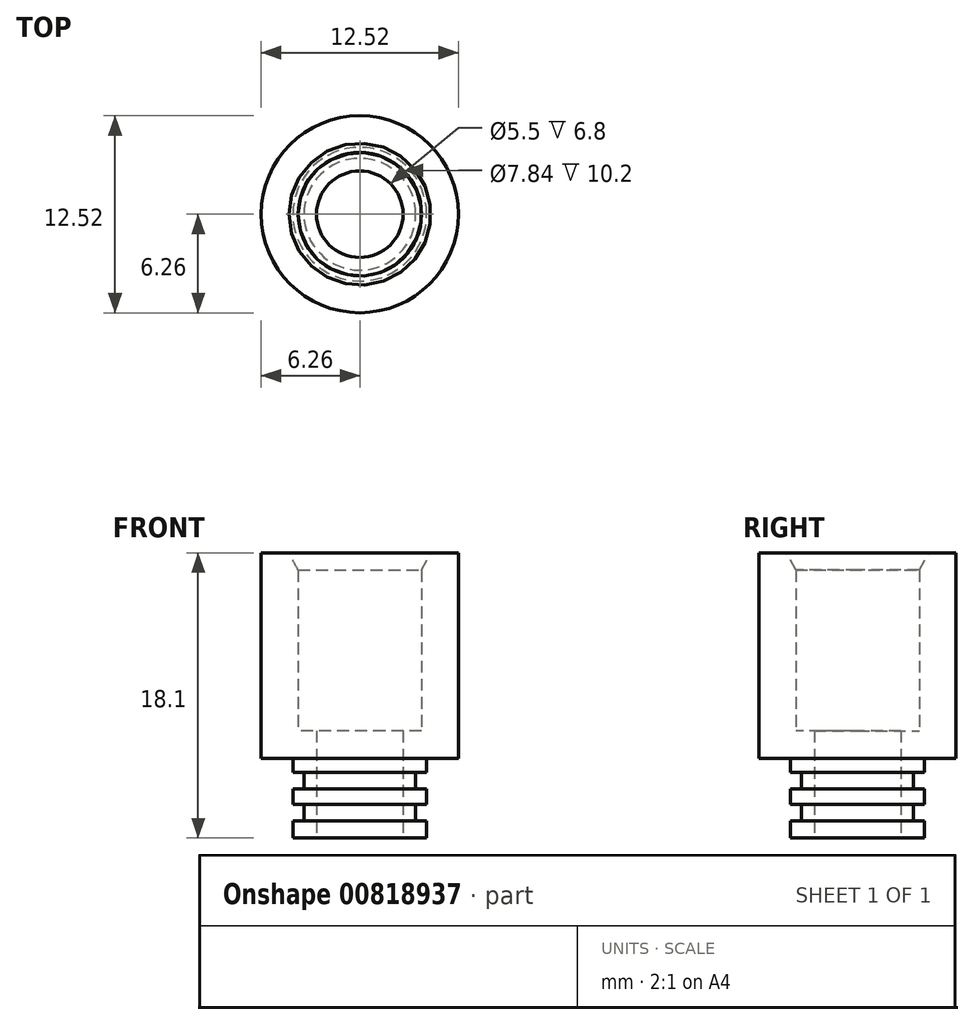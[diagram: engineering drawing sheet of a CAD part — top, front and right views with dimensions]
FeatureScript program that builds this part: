
annotation { "Feature Type Name" : "Feature", "Feature Type Description" : "" }
export const myFeature = defineFeature(function(context is Context, id is Id, definition is map)
    precondition{}
    {
        {
            var Q0;
            Q0=qCreatedBy(makeId("Top.planeOp"),FACE);
            var sketch = newSketch(context, id + "F0", { "sketchPlane" : qUnion([Q0])});
            skCircle(sketch, "E0", {"center": v(0, 0) * mm, "radius": 2.75 * mm});
            skCircle(sketch, "E1.0", {"center": v(0, 0) * mm, "radius": 4.25 * mm});
            skSolve(sketch);
        }
        {
            var Q0;
            Q0 = qSketchRegion(id + "F0", true);
            extrude(context, id + "F1", {"entities" : qUnion([Q0]), "depth" : 1.09 * mm, "offsetDistance" : 25 * mm});
        }
        {
            var Q0;
            Q0=makeQuery(id+"F1.opExtrude","CAP_FACE",FACE,{"disambiguationData":[OSD([sQuery(id+"F0.wireOp",EDGE,"E0"),sQuery(id+"F0.wireOp",EDGE,"E1.0")])],"isStart":false});
            var sketch = newSketch(context, id + "F2", { "sketchPlane" : qUnion([Q0])});
            skCircle(sketch, "E2.0", {"center": v(0, 0) * mm, "radius": 3.55 * mm});
            skSolve(sketch);
        }
        {
            var Q0;
            Q0=makeQuery(id+"F2.imprint","IMPRINT",FACE,{"disambiguationData":[TD([[makeQuery(id+"F2.imprint","IMPRINT",EDGE,{"derivedFrom":sQuery(id+"F2.wireOp",EDGE,"E2.0")}),1.0]])]});
            extrude(context, id + "F3", {"entities" : qUnion([Q0]), "operationType" : NewBodyOperationType.ADD, "depth" : 1.03 * mm, "offsetDistance" : 25 * mm});
        }
        {
            var Q0;
            Q0=makeQuery(id+"F3.opExtrude","CAP_FACE",FACE,{"disambiguationData":[OSD([sQuery(id+"F0.wireOp",EDGE,"E0"),sQuery(id+"F2.wireOp",EDGE,"E2.0")])],"isStart":false});
            var sketch = newSketch(context, id + "F4", { "sketchPlane" : qUnion([Q0])});
            skCircle(sketch, "E3.0", {"center": v(0, 0) * mm, "radius": 4.25 * mm});
            skSolve(sketch);
        }
        {
            var Q0;
            Q0=makeQuery(id+"F4.imprint","IMPRINT",FACE,{"disambiguationData":[TD([[makeQuery(id+"F4.imprint","IMPRINT",EDGE,{"derivedFrom":sQuery(id+"F4.wireOp",EDGE,"E3.0")}),1.0]])]});
            var Q1;
            Q1=makeQuery(id+"F4.imprint","IMPRINT",FACE,{"disambiguationData":[TD([[makeQuery(id+"F4.imprint","IMPRINT",EDGE,{"derivedFrom":makeQuery(id+"F3.opExtrude","CAP_EDGE",EDGE,{"disambiguationData":[OSD([sQuery(id+"F2.wireOp",EDGE,"E2.0")])],"isStart":false})}),1.0]])]});
            extrude(context, id + "F5", {"entities" : qUnion([Q0, Q1]), "operationType" : NewBodyOperationType.ADD, "depth" : 1 * mm, "offsetDistance" : 25 * mm});
        }
        {
            var Q0;
            Q0=makeQuery(id+"F5.opExtrude","CAP_FACE",FACE,{"disambiguationData":[OSD([sQuery(id+"F0.wireOp",EDGE,"E0"),sQuery(id+"F4.wireOp",EDGE,"E3.0")])],"isStart":false});
            var sketch = newSketch(context, id + "F6", { "sketchPlane" : qUnion([Q0])});
            skCircle(sketch, "E4.0", {"center": v(0, 0) * mm, "radius": 3.55 * mm});
            skSolve(sketch);
        }
        {
            var Q0;
            Q0=makeQuery(id+"F6.imprint","IMPRINT",FACE,{"disambiguationData":[TD([[makeQuery(id+"F6.imprint","IMPRINT",EDGE,{"derivedFrom":sQuery(id+"F6.wireOp",EDGE,"E4.0")}),1.0]])]});
            extrude(context, id + "F7", {"entities" : qUnion([Q0]), "operationType" : NewBodyOperationType.ADD, "depth" : 1.03 * mm, "offsetDistance" : 25 * mm});
        }
        {
            var Q0;
            Q0=makeQuery(id+"F7.opExtrude","CAP_FACE",FACE,{"disambiguationData":[OSD([sQuery(id+"F0.wireOp",EDGE,"E0"),sQuery(id+"F6.wireOp",EDGE,"E4.0")])],"isStart":false});
            var sketch = newSketch(context, id + "F8", { "sketchPlane" : qUnion([Q0])});
            skCircle(sketch, "E5.0", {"center": v(0, 0) * mm, "radius": 4.25 * mm});
            skSolve(sketch);
        }
        {
            var Q0;
            Q0=makeQuery(id+"F8.imprint","IMPRINT",FACE,{"disambiguationData":[TD([[makeQuery(id+"F8.imprint","IMPRINT",EDGE,{"derivedFrom":sQuery(id+"F8.wireOp",EDGE,"E5.0")}),1.0]])]});
            var Q1;
            Q1=makeQuery(id+"F8.imprint","IMPRINT",FACE,{"disambiguationData":[TD([[makeQuery(id+"F8.imprint","IMPRINT",EDGE,{"derivedFrom":makeQuery(id+"F7.opExtrude","CAP_EDGE",EDGE,{"disambiguationData":[OSD([sQuery(id+"F6.wireOp",EDGE,"E4.0")])],"isStart":false})}),1.0]])]});
            extrude(context, id + "F9", {"entities" : qUnion([Q0, Q1]), "operationType" : NewBodyOperationType.ADD, "depth" : 0.9 * mm, "offsetDistance" : 25 * mm});
        }
        {
            var Q0;
            Q0=makeQuery(id+"F9.opExtrude","CAP_FACE",FACE,{"disambiguationData":[OSD([sQuery(id+"F0.wireOp",EDGE,"E0"),sQuery(id+"F8.wireOp",EDGE,"E5.0")])],"isStart":false});
            var sketch = newSketch(context, id + "F10", { "sketchPlane" : qUnion([Q0])});
            skCircle(sketch, "E6", {"center": v(0, 0) * mm, "radius": 6.26 * mm});
            skSolve(sketch);
        }
        {
            var Q0;
            Q0=makeQuery(id+"F10.imprint","IMPRINT",FACE,{"disambiguationData":[TD([[makeQuery(id+"F10.imprint","IMPRINT",EDGE,{"derivedFrom":makeQuery(id+"F9.opExtrude","CAP_EDGE",EDGE,{"disambiguationData":[OSD([sQuery(id+"F8.wireOp",EDGE,"E5.0")])],"isStart":false})}),1.0]])]});
            var Q1;
            Q1=makeQuery(id+"F10.imprint","IMPRINT",FACE,{"disambiguationData":[TD([[makeQuery(id+"F10.imprint","IMPRINT",EDGE,{"derivedFrom":sQuery(id+"F10.wireOp",EDGE,"E6")}),1.0]])]});
            extrude(context, id + "F11", {"entities" : qUnion([Q0, Q1]), "operationType" : NewBodyOperationType.ADD, "depth" : 1.75 * mm, "offsetDistance" : 25 * mm});
        }
        {
            var Q0;
            Q0=makeQuery(id+"F11.opExtrude","CAP_FACE",FACE,{"disambiguationData":[OSD([sQuery(id+"F0.wireOp",EDGE,"E0"),sQuery(id+"F10.wireOp",EDGE,"E6")])],"isStart":false});
            var sketch = newSketch(context, id + "F12", { "sketchPlane" : qUnion([Q0])});
            skCircle(sketch, "E7.0", {"center": v(0, 0) * mm, "radius": 3.92 * mm});
            skSolve(sketch);
        }
        {
            var Q0;
            Q0=makeQuery(id+"F12.imprint","IMPRINT",FACE,{"disambiguationData":[TD([[makeQuery(id+"F12.imprint","IMPRINT",EDGE,{"derivedFrom":sQuery(id+"F12.wireOp",EDGE,"E7.0")}),-1.0]])]});
            extrude(context, id + "F13", {"entities" : qUnion([Q0]), "operationType" : NewBodyOperationType.ADD, "depth" : 10.2 * mm, "offsetDistance" : 25 * mm});
        }
        {
            var Q0;
            Q0=makeQuery(id+"F13.opExtrude","CAP_FACE",FACE,{"disambiguationData":[OSD([sQuery(id+"F10.wireOp",EDGE,"E6"),sQuery(id+"F12.wireOp",EDGE,"E7.0")])],"isStart":false});
            var sketch = newSketch(context, id + "F14", { "sketchPlane" : qUnion([Q0])});
            skCircle(sketch, "E8.0", {"center": v(0, 0) * mm, "radius": 4.5 * mm});
            skSolve(sketch);
        }
        {
            var Q0;
            Q0=makeQuery(id+"F14.imprint","IMPRINT",FACE,{"disambiguationData":[TD([[makeQuery(id+"F14.imprint","IMPRINT",EDGE,{"derivedFrom":sQuery(id+"F14.wireOp",EDGE,"E8.0")}),-1.0]])]});
            extrude(context, id + "F15", {"entities" : qUnion([Q0]), "operationType" : NewBodyOperationType.ADD, "depth" : 1.1 * mm, "offsetDistance" : 25 * mm});
        }
        {
            var Q0;
            Q0=qCreatedBy(makeId("Front.planeOp"),FACE);
            var sketch = newSketch(context, id + "F16", { "sketchPlane" : qUnion([Q0])});
            skLineSegment(sketch, "E9", {"start": v(-4.5, 17) * mm, "end": v(-4.5, 18.1) * mm});
            skLineSegment(sketch, "E10", {"start": v(-4.5, 18.1) * mm, "end": v(-3.92, 17) * mm});
            skLineSegment(sketch, "E11", {"start": v(-3.92, 17) * mm, "end": v(-4.5, 17) * mm});
            skSolve(sketch);
        }
        {
            var Q0;
            Q0=makeQuery(id+"F16.imprint","IMPRINT",FACE,{"disambiguationData":[TD([[makeQuery(id+"F16.imprint","IMPRINT",EDGE,{"derivedFrom":sQuery(id+"F16.wireOp",EDGE,"E9")}),-1.0]])]});
            var Q1;
            Q1=makeQuery(id+"F13.opExtrude","CAP_EDGE",EDGE,{"disambiguationData":[OSD([sQuery(id+"F12.wireOp",EDGE,"E7.0")])],"isStart":false});
            revolve(context, id + "F17", {"operationType" : NewBodyOperationType.ADD, "surfaceOperationType" : NewSurfaceOperationType.NEW, "entities" : qUnion([Q0]), "axis" : qUnion([Q1]), "revolveType" : RevolveType.FULL});
        }
    });
